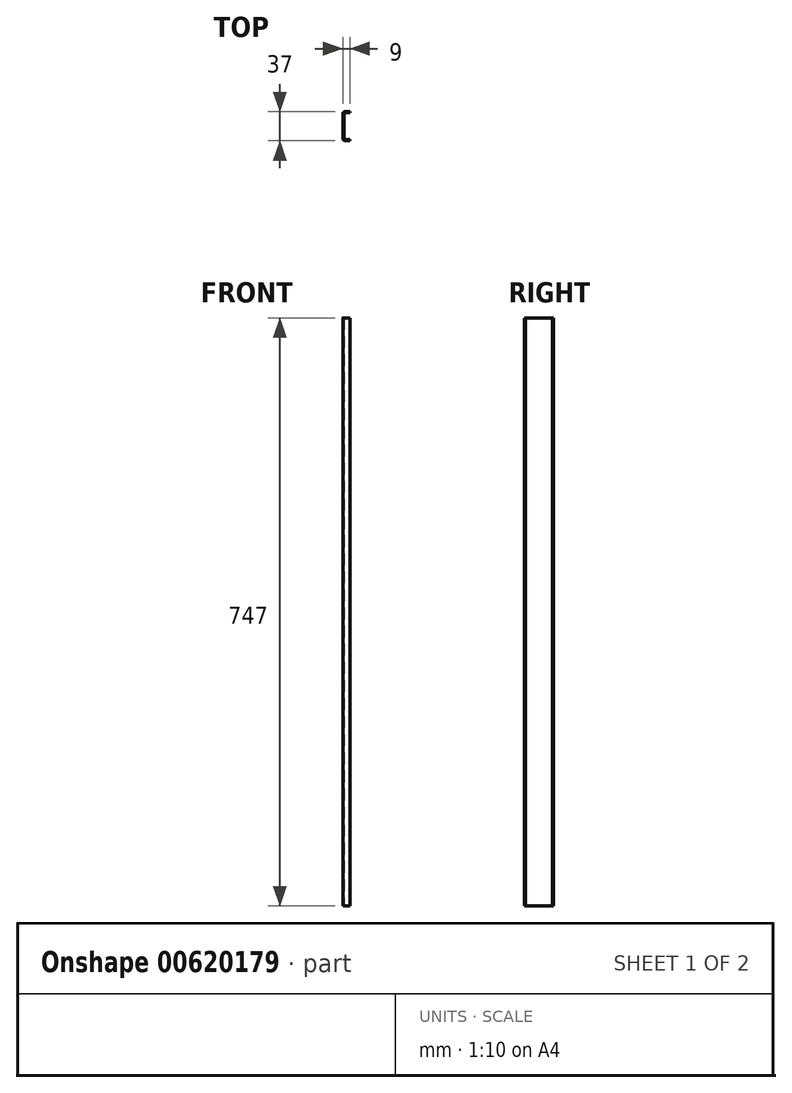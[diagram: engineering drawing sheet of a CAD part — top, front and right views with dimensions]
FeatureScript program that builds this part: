
annotation { "Feature Type Name" : "Feature", "Feature Type Description" : "" }
export const myFeature = defineFeature(function(context is Context, id is Id, definition is map)
    precondition{}
    {
        {
            var Q0;
            Q0=qCreatedBy(makeId("Top.planeOp"),FACE);
            var sketch = newSketch(context, id + "F0", { "sketchPlane" : qUnion([Q0])});
            skLineSegment(sketch, "E0", {"start": v(9, 18.5) * mm, "end": v(3, 18.5) * mm});
            skLineSegment(sketch, "E1", {"start": v(0, 15.5) * mm, "end": v(0, 0) * mm});
            skPoint(sketch, "E2.visualSharp", {"position": v(0, 18.5) * mm});
            skArc(sketch, "E2.filletArc", {"start": v(3, 18.5) * mm, "mid": v(0.88, 17.62) * mm, "end": v(0, 15.5) * mm});
            skLineSegment(sketch, "E3.MirrorCS", {"start": v(0, -15.5) * mm, "end": v(0, 0) * mm});
            skArc(sketch, "E4.MirrorCS", {"start": v(3, -18.5) * mm, "mid": v(0.88, -17.62) * mm, "end": v(0, -15.5) * mm});
            skLineSegment(sketch, "E5.MirrorCS", {"start": v(9, -18.5) * mm, "end": v(3, -18.5) * mm});
            skLineSegment(sketch, "E6.0", {"start": v(9, -17) * mm, "end": v(3, -17) * mm});
            skArc(sketch, "E6.1", {"start": v(3, -17) * mm, "mid": v(1.94, -16.56) * mm, "end": v(1.5, -15.5) * mm});
            skLineSegment(sketch, "E6.2", {"start": v(9, 17) * mm, "end": v(3, 17) * mm});
            skArc(sketch, "E6.3", {"start": v(3, 17) * mm, "mid": v(1.94, 16.56) * mm, "end": v(1.5, 15.5) * mm});
            skLineSegment(sketch, "E6.4", {"start": v(1.5, 15.5) * mm, "end": v(1.5, 0) * mm});
            skLineSegment(sketch, "E6.5", {"start": v(1.5, -15.5) * mm, "end": v(1.5, 0) * mm});
            skLineSegment(sketch, "E7", {"start": v(9, 18.5) * mm, "end": v(9, 17) * mm});
            skLineSegment(sketch, "E8", {"start": v(9, -17) * mm, "end": v(9, -18.5) * mm});
            skSolve(sketch);
        }
        {
            var Q0;
            Q0=makeQuery(id+"F0.imprint","IMPRINT",FACE,{"disambiguationData":[TD([[makeQuery(id+"F0.imprint","IMPRINT",EDGE,{"derivedFrom":sQuery(id+"F0.wireOp",EDGE,"E0")}),1.0]])]});
            extrude(context, id + "F1", {"entities" : qUnion([Q0]), "endBound" : BoundingType.SYMMETRIC, "depth" : 747 * mm, "offsetDistance" : 25 * mm});
        }
    });
